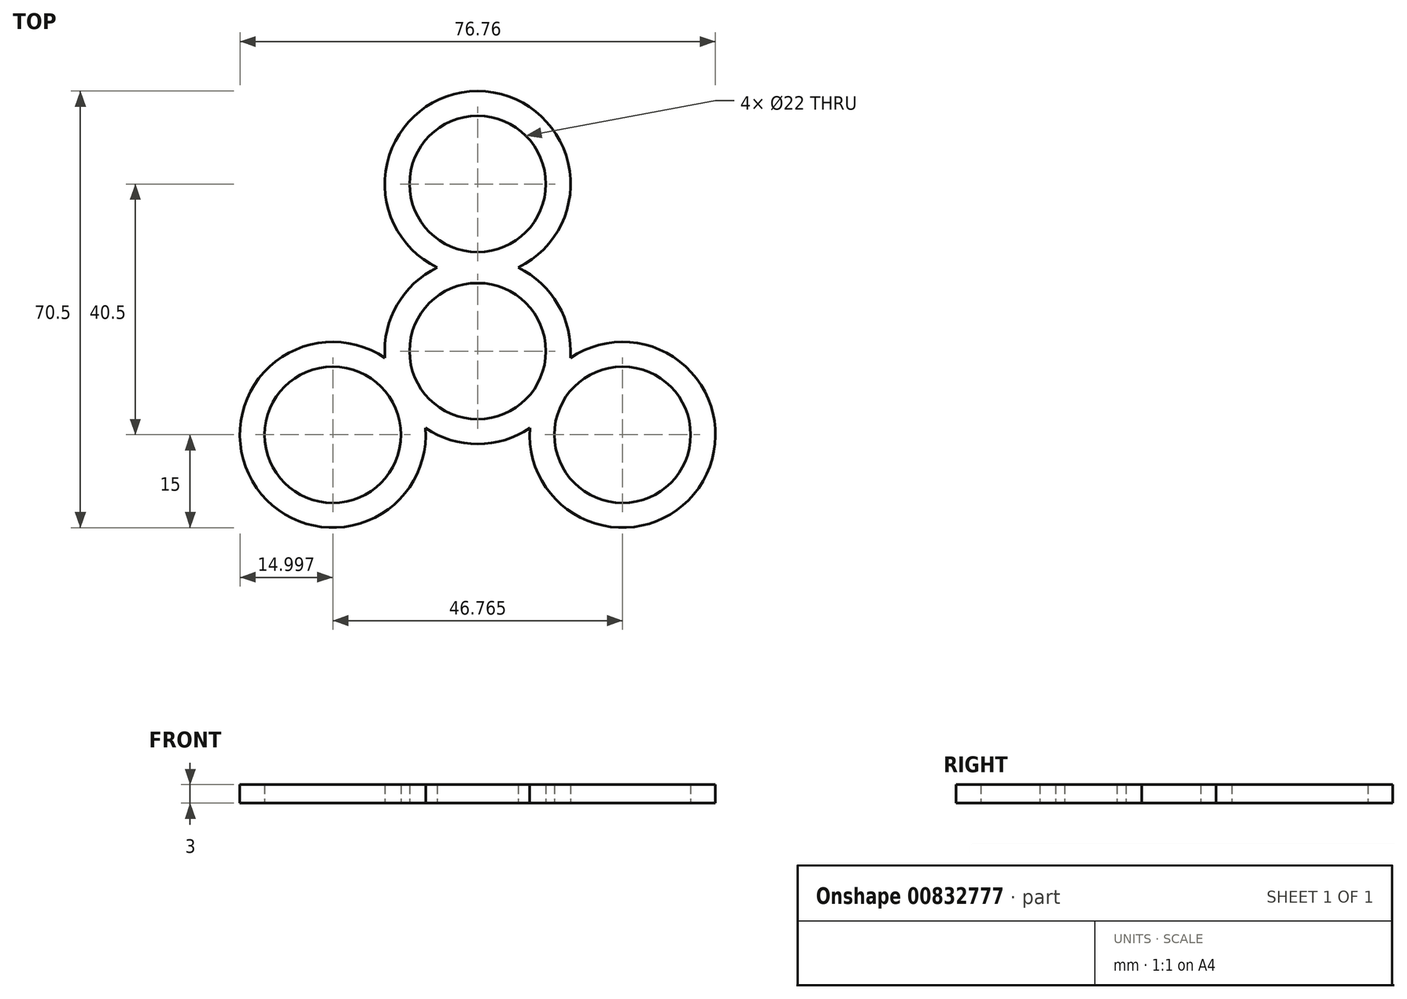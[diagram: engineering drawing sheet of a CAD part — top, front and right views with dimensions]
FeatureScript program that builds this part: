
annotation { "Feature Type Name" : "Feature", "Feature Type Description" : "" }
export const myFeature = defineFeature(function(context is Context, id is Id, definition is map)
    precondition{}
    {
        {
            var Q0;
            Q0=qCreatedBy(makeId("Top.planeOp"),FACE);
            var sketch = newSketch(context, id + "F0", { "sketchPlane" : qUnion([Q0])});
            skArc(sketch, "E0", {"start": v(9.53, 5.5) * mm, "mid": v(0, 11) * mm, "end": v(-9.53, 5.5) * mm});
            skArc(sketch, "E1", {"start": v(13, 7.5) * mm, "mid": v(10.21, 10.98) * mm, "end": v(6.54, 13.5) * mm});
            skLineSegment(sketch, "E2", {"start": v(0, 0) * mm, "end": v(0, 27) * mm});
            skCircle(sketch, "E3", {"center": v(0, 27) * mm, "radius": 11 * mm});
            skArc(sketch, "E4", {"start": v(6.54, 13.5) * mm, "mid": v(0, 42) * mm, "end": v(-6.54, 13.5) * mm});
            skArc(sketch, "E5.trimOffspring", {"start": v(-6.54, 13.5) * mm, "mid": v(-10.21, 10.98) * mm, "end": v(-13, 7.5) * mm});
            skCircle(sketch, "E6.1.0", {"center": v(-23.38, -13.5) * mm, "radius": 11 * mm});
            skArc(sketch, "E6.1.1", {"start": v(-14.96, -1.09) * mm, "mid": v(-36.37, -21) * mm, "end": v(-8.42, -12.41) * mm});
            skArc(sketch, "E6.1.2", {"start": v(-8.42, -12.41) * mm, "mid": v(-4.4, -14.34) * mm, "end": v(0, -15) * mm});
            skArc(sketch, "E6.1.3", {"start": v(-9.53, 5.5) * mm, "mid": v(-9.53, -5.5) * mm, "end": v(0, -11) * mm});
            skArc(sketch, "E6.1.4", {"start": v(-13, 7.5) * mm, "mid": v(-14.62, 3.35) * mm, "end": v(-14.96, -1.09) * mm});
            skCircle(sketch, "E6.2.0", {"center": v(23.38, -13.5) * mm, "radius": 11 * mm});
            skArc(sketch, "E6.2.1", {"start": v(8.42, -12.41) * mm, "mid": v(36.37, -21) * mm, "end": v(14.96, -1.09) * mm});
            skArc(sketch, "E6.2.2", {"start": v(14.96, -1.09) * mm, "mid": v(14.62, 3.35) * mm, "end": v(13, 7.5) * mm});
            skArc(sketch, "E6.2.3", {"start": v(0, -11) * mm, "mid": v(9.53, -5.5) * mm, "end": v(9.53, 5.5) * mm});
            skArc(sketch, "E6.2.4", {"start": v(0, -15) * mm, "mid": v(4.4, -14.34) * mm, "end": v(8.42, -12.41) * mm});
            skSolve(sketch);
        }
        {
            var Q0;
            Q0 = qSketchRegion(id + "F0", true);
            extrude(context, id + "F1", {"entities" : qUnion([Q0]), "depth" : 3 * mm, "offsetDistance" : 25 * mm});
        }
    });
